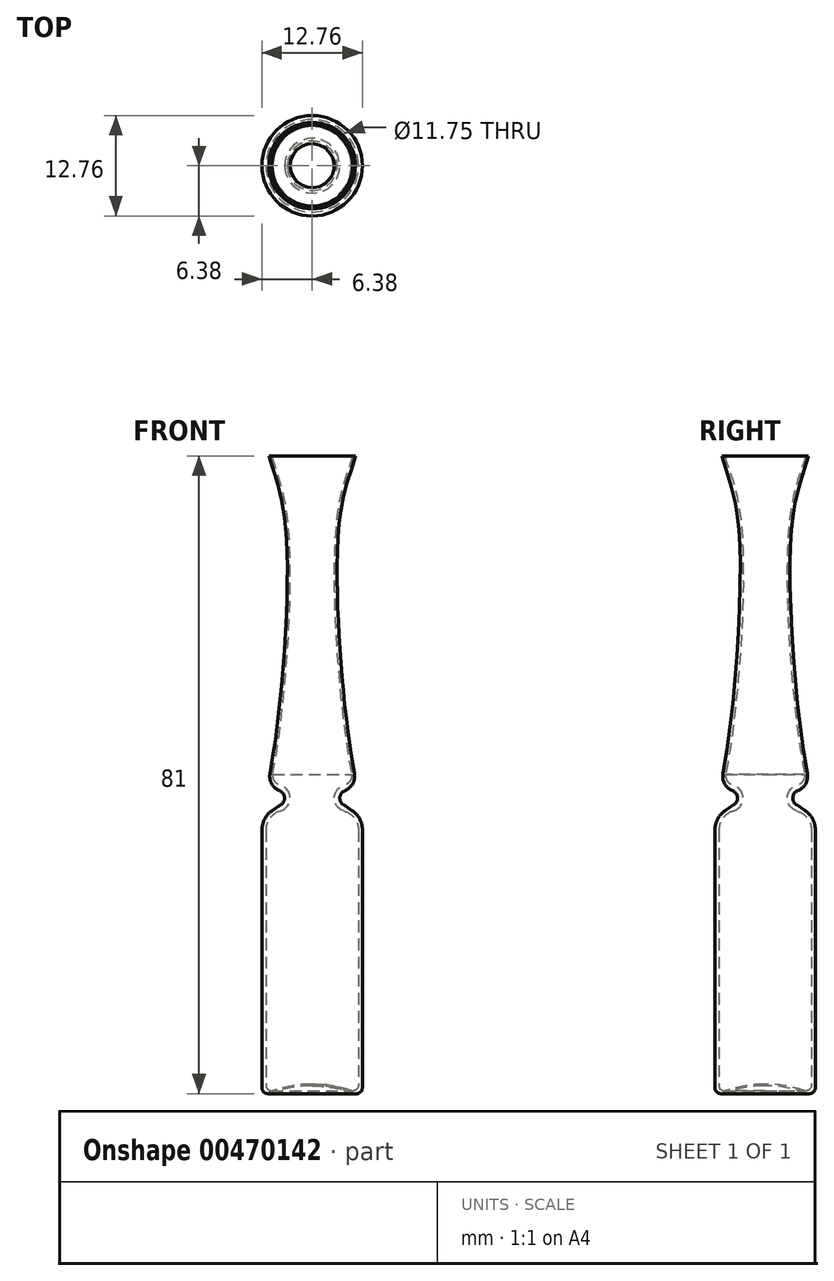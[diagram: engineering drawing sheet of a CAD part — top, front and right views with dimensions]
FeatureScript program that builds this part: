
annotation { "Feature Type Name" : "Feature", "Feature Type Description" : "" }
export const myFeature = defineFeature(function(context is Context, id is Id, definition is map)
    precondition{}
    {
        {
            var Q0;
            Q0=qCreatedBy(makeId("Front.planeOp"),FACE);
            var sketch = newSketch(context, id + "F0", { "sketchPlane" : qUnion([Q0])});
            skLineSegment(sketch, "E0", {"start": v(0, 0) * mm, "end": v(0, 82.71) * mm, "construction": true});
            skLineSegment(sketch, "E1", {"start": v(6.38, 0.75) * mm, "end": v(6.38, 33.5) * mm});
            skLineSegment(sketch, "E2", {"start": v(5.02, 36) * mm, "end": v(3.95, 36.71) * mm});
            skLineSegment(sketch, "E3", {"start": v(5.5, 81) * mm, "end": v(0, 81) * mm});
            skArc(sketch, "E4.filletArc", {"start": v(6.38, 33.5) * mm, "mid": v(6.02, 34.92) * mm, "end": v(5.02, 36) * mm});
            skPoint(sketch, "E5.visualSharp", {"position": v(2.75, 37.5) * mm});
            skArc(sketch, "E5.filletArc", {"start": v(4.13, 38.48) * mm, "mid": v(3.5, 37.65) * mm, "end": v(3.95, 36.71) * mm});
            skFitSpline(sketch, "E6", {"points": [v(5.5, 39.9) * mm, v(3.31, 71.2) * mm, v(5.5, 81) * mm], "startDerivative": vector(-8.76, 47.12) * mm, "endDerivative": vector(9.68, 30.82) * mm});
            skArc(sketch, "E7.filletArc", {"start": v(4.13, 38.48) * mm, "mid": v(5.14, 39.36) * mm, "end": v(5.36, 40.68) * mm});
            skLineSegment(sketch, "E8", {"start": v(3.5, 40.16) * mm, "end": v(3.5, 36.18) * mm, "construction": true});
            skLineSegment(sketch, "E9", {"start": v(-6.37, 0) * mm, "end": v(5.63, 0) * mm, "construction": true});
            skArc(sketch, "E10", {"start": v(5.37, 0.05) * mm, "mid": v(6.05, 0.14) * mm, "end": v(6.38, 0.75) * mm});
            skArc(sketch, "E11", {"start": v(5.37, 0.05) * mm, "mid": v(2.73, 0.76) * mm, "end": v(0, 1) * mm});
            skLineSegment(sketch, "E12", {"start": v(-0.93, 1) * mm, "end": v(1.1, 1) * mm, "construction": true});
            skArc(sketch, "E13.0", {"start": v(4.96, 0.4) * mm, "mid": v(2.5, 1) * mm, "end": v(0, 1.2) * mm});
            skLineSegment(sketch, "E14.0", {"start": v(5.88, 1.07) * mm, "end": v(5.88, 33.5) * mm});
            skPoint(sketch, "E15.visualSharp", {"position": v(5.88, 0.06) * mm});
            skArc(sketch, "E15.filletArc", {"start": v(4.96, 0.4) * mm, "mid": v(5.58, 0.5) * mm, "end": v(5.88, 1.07) * mm});
            skArc(sketch, "E16.0", {"start": v(4.06, 39.19) * mm, "mid": v(2.8, 37.55) * mm, "end": v(4.04, 35.9) * mm});
            skArc(sketch, "E17", {"start": v(4.04, 35.9) * mm, "mid": v(5.37, 35.01) * mm, "end": v(5.88, 33.5) * mm});
            skFitSpline(sketch, "E18.0", {"points": [v(5.16, 39.83) * mm, v(4.79, 41.8) * mm, v(4.14, 46.04) * mm, v(3.4, 52.83) * mm, v(2.94, 59.57) * mm, v(2.8, 64.75) * mm, v(2.82, 68.38) * mm, v(2.9, 70.4) * mm, v(3, 71.83) * mm, v(3.13, 73.14) * mm, v(3.43, 75.18) * mm, v(4.06, 77.67) * mm, v(4.76, 79.82) * mm, v(5.17, 81.1) * mm]});
            skArc(sketch, "E19", {"start": v(4.06, 39.19) * mm, "mid": v(4.82, 39.75) * mm, "end": v(5, 40.67) * mm});
            skLineSegment(sketch, "E20", {"start": v(0, 1.2) * mm, "end": v(0, 1) * mm});
            skSolve(sketch);
        }
        {
            var Q0;
            Q0 = qSketchRegion(id + "F0", true);
            var Q1;
            Q1=sQuery(id+"F0.wireOp",EDGE,"E0");
            revolve(context, id + "F1", {"entities" : qUnion([Q0]), "axis" : qUnion([Q1]), "revolveType" : RevolveType.FULL});
        }
    });
